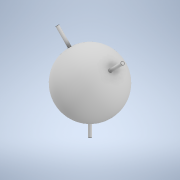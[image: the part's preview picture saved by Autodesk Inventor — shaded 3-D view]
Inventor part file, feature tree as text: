
AUTODESK INVENTOR PART (.ipt)
format: ipt  version: 2022 (Build 260153000, 153)  size: 166,912 bytes
history: native  units: in
note: dims shown in document units (in); Inventor stores cm internally (conversion verified against a paired STEP export)
features: sketch x8, extrude x5, revolve x3
ambient origin geometry x8: Origin, YZ Plane, XZ Plane, XY Plane, X Axis, Y Axis, Z Axis, Center Point
bodies: Solid1 (feature_tree)
feature tree (16):
  revolve  "Revolution1"  Angle=180.0deg
  extrude  "Extrusion1"  Depth=1.3in
  extrude  "Extrusion2"  Depth=4.0in TaperAngle=0.0deg
  revolve  "Revolution2"  [1 undecoded]
  extrude  "Extrusion6"  Depth=4.0in TaperAngle=0.0deg
  extrude  "Extrusion7"  Depth=0.932in TaperAngle=0.0deg
  extrude  "Extrusion8"  Depth=0.932in TaperAngle=0.0deg
  revolve  "Revolution4"  [1 undecoded]
  sketch  "Sketch1"  dims[d2=1.25in d3=180.0deg]
  sketch  "Sketch2"  dims[d4=90.0deg d5=1.3in]
  sketch  "Sketch3"  dims[d6=2.5in d7=4.0in d8=0.0in]
  sketch  "Sketch4"  dims[d9=0.125in d10=0.932in d11=0.0in]
  sketch  "Sketch9"  dims[d12=90.0deg d22=4.0in d23=0.0in]
  sketch  "Sketch10"  dims[d24=0.125in d25=0.932in d26=0.0in]
  sketch  "Sketch11"  dims[d27=0.125in d28=0.932in d29=0.0in]
  sketch  "Sketch12"  dims[d30=90.0deg]
note: 2 required parameter values undecoded (feature->parameter linkage not recoverable at this tier; creation-order binding heuristic only, values carry confidence <= 0.55)